annotation { "Feature Type Name" : "Feature", "Feature Type Description" : "" }
export const myFeature = defineFeature(function(context is Context, id is Id, definition is map)
    precondition{}
    {
        {
            var Q0;
            Q0=qCreatedBy(makeId("Top.planeOp"),FACE);
            var sketch = newSketch(context, id + "F0", { "sketchPlane" : qUnion([Q0])});
            skLineSegment(sketch, "E0.bottom", {"start": v(-4999.5, -4999.5) * mm, "end": v(4999.5, -4999.5) * mm});
            skLineSegment(sketch, "E0.top", {"start": v(-4999.5, 4999.5) * mm, "end": v(4999.5, 4999.5) * mm});
            skLineSegment(sketch, "E0.left", {"start": v(-4999.5, -4999.5) * mm, "end": v(-4999.5, 4999.5) * mm});
            skLineSegment(sketch, "E0.right", {"start": v(4999.5, -4999.5) * mm, "end": v(4999.5, 4999.5) * mm});
            skLineSegment(sketch, "E1", {"start": v(-4999.5, 4999.5) * mm, "end": v(4999.5, -4999.5) * mm, "construction": true});
            skSolve(sketch);
        }
        {
            var Q0;
            Q0=makeQuery(id+"F0.imprint","IMPRINT",FACE,{"disambiguationData":[TD([[makeQuery(id+"F0.imprint","IMPRINT",EDGE,{"derivedFrom":sQuery(id+"F0.wireOp",EDGE,"E0.bottom")}),1.0]])]});
            extrude(context, id + "F1", {"entities" : qUnion([Q0]), "endBound" : BoundingType.SYMMETRIC, "depth" : 9999 * mm, "offsetDistance" : 25 * mm});
        }
        {
            var Q0;
            Q0=qCreatedBy(makeId("Front.planeOp"),FACE);
            var sketch = newSketch(context, id + "F2", { "sketchPlane" : qUnion([Q0])});
            skLineSegment(sketch, "E2", {"start": v(0, 0) * mm, "end": v(0, 17.55) * mm});
            skLineSegment(sketch, "E3", {"start": v(0, 63.5) * mm, "end": v(-40, 63.5) * mm, "construction": true});
            skLineSegment(sketch, "E4", {"start": v(-40, 77.05) * mm, "end": v(-40, 49.95) * mm});
            skLineSegment(sketch, "E5", {"start": v(-27.76, 35.2) * mm, "end": v(-12.24, 32.3) * mm});
            skLineSegment(sketch, "E6", {"start": v(-27.76, 91.8) * mm, "end": v(-12.24, 94.7) * mm});
            skLineSegment(sketch, "E7.trimOffspring", {"start": v(0, 109.45) * mm, "end": v(0, 127) * mm});
            skLineSegment(sketch, "E8", {"start": v(0, 97) * mm, "end": v(0, 63.5) * mm, "construction": true});
            skLineSegment(sketch, "E9", {"start": v(0, 63.5) * mm, "end": v(0, 30) * mm, "construction": true});
            skPoint(sketch, "E10.visualSharp", {"position": v(0, 97) * mm});
            skArc(sketch, "E10.filletArc", {"start": v(-12.24, 94.7) * mm, "mid": v(-3.46, 99.87) * mm, "end": v(0, 109.45) * mm});
            skPoint(sketch, "E11.visualSharp", {"position": v(-40, 89.5) * mm});
            skArc(sketch, "E11.filletArc", {"start": v(-27.76, 91.8) * mm, "mid": v(-36.54, 86.63) * mm, "end": v(-40, 77.05) * mm});
            skPoint(sketch, "E12.visualSharp", {"position": v(-40, 37.5) * mm});
            skArc(sketch, "E12.filletArc", {"start": v(-40, 49.95) * mm, "mid": v(-36.54, 40.37) * mm, "end": v(-27.76, 35.2) * mm});
            skPoint(sketch, "E13.visualSharp", {"position": v(0, 30) * mm});
            skArc(sketch, "E13.filletArc", {"start": v(0, 17.55) * mm, "mid": v(-3.46, 27.13) * mm, "end": v(-12.24, 32.3) * mm});
            skLineSegment(sketch, "E14.0", {"start": v(-4, 109.45) * mm, "end": v(-4, 127) * mm});
            skArc(sketch, "E14.1", {"start": v(-12.97, 98.64) * mm, "mid": v(-6.54, 102.42) * mm, "end": v(-4, 109.45) * mm});
            skLineSegment(sketch, "E14.2", {"start": v(-28.5, 95.73) * mm, "end": v(-12.97, 98.64) * mm});
            skArc(sketch, "E14.3", {"start": v(-28.5, 95.73) * mm, "mid": v(-39.62, 89.19) * mm, "end": v(-44, 77.05) * mm});
            skLineSegment(sketch, "E14.4", {"start": v(-44, 77.05) * mm, "end": v(-44, 49.95) * mm});
            skLineSegment(sketch, "E14.5", {"start": v(-4, 0) * mm, "end": v(-4, 17.55) * mm});
            skArc(sketch, "E14.6", {"start": v(-4, 17.55) * mm, "mid": v(-6.54, 24.58) * mm, "end": v(-12.97, 28.36) * mm});
            skLineSegment(sketch, "E14.7", {"start": v(-28.5, 31.27) * mm, "end": v(-12.97, 28.36) * mm});
            skArc(sketch, "E14.8", {"start": v(-44, 49.95) * mm, "mid": v(-39.62, 37.81) * mm, "end": v(-28.5, 31.27) * mm});
            skLineSegment(sketch, "E15", {"start": v(0, 127) * mm, "end": v(-4, 127) * mm});
            skLineSegment(sketch, "E16", {"start": v(-4, 0) * mm, "end": v(0, 0) * mm});
            skSolve(sketch);
        }
        {
            var Q0;
            Q0=qCreatedBy(makeId("Front.planeOp"),FACE);
            cPlane(context, id + "F3", {"entities" : qUnion([Q0]), "cplaneType" : CPlaneType.OFFSET, "offset" : 60 * mm, "width" : 150 * mm, "height" : 150 * mm});
        }
        {
            var Q0;
            Q0=qCreatedBy(id+"F3.planeOp",FACE);
            var sketch = newSketch(context, id + "F4", { "sketchPlane" : qUnion([Q0])});
            skLineSegment(sketch, "E17.0", {"start": v(0, 0) * mm, "end": v(0, 17.55) * mm});
            skLineSegment(sketch, "E17.1", {"start": v(0, 63.5) * mm, "end": v(-40, 63.5) * mm, "construction": true});
            skLineSegment(sketch, "E17.2", {"start": v(-40, 77.05) * mm, "end": v(-40, 49.95) * mm, "construction": true});
            skLineSegment(sketch, "E17.3", {"start": v(-27.76, 35.2) * mm, "end": v(-12.24, 32.3) * mm, "construction": true});
            skLineSegment(sketch, "E17.4", {"start": v(-27.76, 91.8) * mm, "end": v(-12.24, 94.7) * mm, "construction": true});
            skLineSegment(sketch, "E17.5", {"start": v(0, 109.45) * mm, "end": v(0, 127) * mm});
            skLineSegment(sketch, "E17.6", {"start": v(0, 97) * mm, "end": v(0, 63.5) * mm});
            skLineSegment(sketch, "E17.7", {"start": v(0, 63.5) * mm, "end": v(0, 30) * mm});
            skPoint(sketch, "E17.8", {"position": v(0, 97) * mm});
            skArc(sketch, "E17.9", {"start": v(-12.24, 94.7) * mm, "mid": v(-3.46, 99.87) * mm, "end": v(0, 109.45) * mm});
            skPoint(sketch, "E17.10", {"position": v(-40, 89.5) * mm});
            skArc(sketch, "E17.11", {"start": v(-27.76, 91.8) * mm, "mid": v(-36.54, 86.63) * mm, "end": v(-40, 77.05) * mm, "construction": true});
            skPoint(sketch, "E17.12", {"position": v(-40, 37.5) * mm});
            skArc(sketch, "E17.13", {"start": v(-40, 49.95) * mm, "mid": v(-36.54, 40.37) * mm, "end": v(-27.76, 35.2) * mm, "construction": true});
            skPoint(sketch, "E17.14", {"position": v(0, 30) * mm});
            skArc(sketch, "E17.15", {"start": v(0, 17.55) * mm, "mid": v(-3.46, 27.13) * mm, "end": v(-12.24, 32.3) * mm});
            skLineSegment(sketch, "E17.16", {"start": v(-4, 109.45) * mm, "end": v(-4, 127) * mm});
            skArc(sketch, "E17.17", {"start": v(-12.42, 98.76) * mm, "mid": v(-6.36, 102.64) * mm, "end": v(-4, 109.45) * mm});
            skLineSegment(sketch, "E17.18", {"start": v(-28.5, 95.73) * mm, "end": v(-12.97, 98.64) * mm, "construction": true});
            skArc(sketch, "E17.19", {"start": v(-28.5, 95.73) * mm, "mid": v(-39.62, 89.19) * mm, "end": v(-44, 77.05) * mm, "construction": true});
            skLineSegment(sketch, "E17.20", {"start": v(-44, 77.05) * mm, "end": v(-44, 49.95) * mm, "construction": true});
            skLineSegment(sketch, "E17.21", {"start": v(-4, 0) * mm, "end": v(-4, 17.55) * mm});
            skArc(sketch, "E17.22", {"start": v(-4, 17.55) * mm, "mid": v(-6.36, 24.36) * mm, "end": v(-12.42, 28.24) * mm});
            skLineSegment(sketch, "E17.23", {"start": v(-28.5, 31.27) * mm, "end": v(-12.97, 28.36) * mm, "construction": true});
            skArc(sketch, "E17.24", {"start": v(-44, 49.95) * mm, "mid": v(-39.62, 37.81) * mm, "end": v(-28.5, 31.27) * mm, "construction": true});
            skLineSegment(sketch, "E17.25", {"start": v(0, 127) * mm, "end": v(-4, 127) * mm});
            skLineSegment(sketch, "E17.26", {"start": v(-4, 0) * mm, "end": v(0, 0) * mm});
            skLineSegment(sketch, "E18", {"start": v(-12.24, 32.3) * mm, "end": v(-33.69, 36.32) * mm});
            skLineSegment(sketch, "E19", {"start": v(-50, 55.97) * mm, "end": v(-50, 63.5) * mm});
            skLineSegment(sketch, "E20", {"start": v(-12.24, 94.7) * mm, "end": v(-33.69, 90.68) * mm});
            skLineSegment(sketch, "E21", {"start": v(-50, 71.03) * mm, "end": v(-50, 63.5) * mm});
            skLineSegment(sketch, "E22", {"start": v(-12.42, 98.76) * mm, "end": v(-35.16, 93.26) * mm});
            skLineSegment(sketch, "E23", {"start": v(-52, 71.88) * mm, "end": v(-52, 55.12) * mm});
            skLineSegment(sketch, "E24", {"start": v(-35.16, 33.74) * mm, "end": v(-12.42, 28.24) * mm});
            skLineSegment(sketch, "E25", {"start": v(-50, 87.62) * mm, "end": v(-50.47, 89.57) * mm, "construction": true});
            skPoint(sketch, "E26.orphan", {"position": v(-12.97, 98.64) * mm});
            skLineSegment(sketch, "E27", {"start": v(-50, 39.38) * mm, "end": v(-50.47, 37.43) * mm, "construction": true});
            skPoint(sketch, "E28.orphan", {"position": v(-12.97, 28.36) * mm});
            skPoint(sketch, "E29.visualSharp", {"position": v(-50, 87.63) * mm});
            skArc(sketch, "E29.filletArc", {"start": v(-33.69, 90.68) * mm, "mid": v(-45.4, 83.8) * mm, "end": v(-50, 71.03) * mm});
            skPoint(sketch, "E30.visualSharp", {"position": v(-50, 39.38) * mm});
            skArc(sketch, "E30.filletArc", {"start": v(-50, 55.97) * mm, "mid": v(-45.4, 43.2) * mm, "end": v(-33.69, 36.32) * mm});
            skPoint(sketch, "E31.visualSharp", {"position": v(-52, 89.2) * mm});
            skArc(sketch, "E31.filletArc", {"start": v(-35.16, 93.26) * mm, "mid": v(-47.29, 85.49) * mm, "end": v(-52, 71.88) * mm});
            skPoint(sketch, "E32.visualSharp", {"position": v(-52, 37.8) * mm});
            skArc(sketch, "E32.filletArc", {"start": v(-52, 55.12) * mm, "mid": v(-47.29, 41.51) * mm, "end": v(-35.16, 33.74) * mm});
            skSolve(sketch);
        }
        {
            var Q0;
            Q0 = qSketchRegion(id + "F2", true);
            var Q1;
            Q1 = qSketchRegion(id + "F4", true);
            loft(context, id + "F5", {"sheetProfilesArray" : [{ "sheetProfileEntities" : qUnion([Q0]) }, { "sheetProfileEntities" : qUnion([Q1]) }]});
        }
        {
            var Q0;
            Q0=makeQuery(id+"F5.opLoft","CAP_FACE",FACE,{"disambiguationData":[OSD([makeQuery(id+"F4.imprint","IMPRINT",FACE,{"disambiguationData":[TD([[makeQuery(id+"F4.imprint","IMPRINT",EDGE,{"derivedFrom":sQuery(id+"F4.wireOp",EDGE,"E17.0")}),1.0]])]})])],"isStart":true});
            var Q1;
            Q1=makeQuery(id+"F5.opLoft","CAP_FACE",FACE,{"disambiguationData":[OSD([makeQuery(id+"F2.imprint","IMPRINT",FACE,{"disambiguationData":[TD([[makeQuery(id+"F2.imprint","IMPRINT",EDGE,{"derivedFrom":sQuery(id+"F2.wireOp",EDGE,"E2")}),1.0]])]})])],"isStart":true});
            cPlane(context, id + "F6", {"entities" : qUnion([Q0, Q1]), "cplaneType" : CPlaneType.MID_PLANE, "offset" : 25 * mm, "width" : 150 * mm, "height" : 150 * mm});
        }
        {
            var Q0;
            Q0=qCreatedBy(id+"F6.planeOp",FACE);
            var sketch = newSketch(context, id + "F7", { "sketchPlane" : qUnion([Q0])});
            skLineSegment(sketch, "E33.0", {"start": v(0, 109.45) * mm, "end": v(0, 127) * mm, "construction": true});
            skLineSegment(sketch, "E34", {"start": v(0, 120.76) * mm, "end": v(0, 118.22) * mm});
            skLineSegment(sketch, "E35", {"start": v(0, 120.76) * mm, "end": v(-2, 120.76) * mm});
            skLineSegment(sketch, "E36", {"start": v(-2, 120.76) * mm, "end": v(-5, 123.37) * mm});
            skLineSegment(sketch, "E37", {"start": v(0, 118.22) * mm, "end": v(-5, 118.22) * mm});
            skLineSegment(sketch, "E38", {"start": v(-5, 118.22) * mm, "end": v(-5, 123.37) * mm});
            skLineSegment(sketch, "E39", {"start": v(0, 127) * mm, "end": v(0, 0) * mm, "construction": true});
            skLineSegment(sketch, "E40", {"start": v(0, 63.5) * mm, "end": v(-27.8, 63.5) * mm, "construction": true});
            skLineSegment(sketch, "E41.MirrorCS", {"start": v(0, 6.24) * mm, "end": v(-2, 6.24) * mm});
            skLineSegment(sketch, "E42.MirrorCS", {"start": v(0, 8.78) * mm, "end": v(-5, 8.78) * mm});
            skLineSegment(sketch, "E43.MirrorCS", {"start": v(-2, 6.24) * mm, "end": v(-5, 3.63) * mm});
            skLineSegment(sketch, "E44.MirrorCS", {"start": v(0, 6.24) * mm, "end": v(0, 8.78) * mm});
            skLineSegment(sketch, "E45.MirrorCS", {"start": v(-5, 8.78) * mm, "end": v(-5, 3.63) * mm});
            skSolve(sketch);
        }
        {
            var Q0;
            Q0=makeQuery(id+"F7.imprint","IMPRINT",FACE,{"disambiguationData":[TD([[makeQuery(id+"F7.imprint","IMPRINT",EDGE,{"derivedFrom":sQuery(id+"F7.wireOp",EDGE,"E34")}),-1.0]])]});
            var Q1;
            Q1=sQuery(id+"F7.wireOp",EDGE,"E37");
            revolve(context, id + "F8", {"operationType" : NewBodyOperationType.REMOVE, "surfaceOperationType" : NewSurfaceOperationType.NEW, "entities" : qUnion([Q0]), "axis" : qUnion([Q1]), "revolveType" : RevolveType.FULL, "oppositeDirection" : true});
        }
        {
            var Q0;
            Q0=makeQuery(id+"F7.imprint","IMPRINT",FACE,{"disambiguationData":[TD([[makeQuery(id+"F7.imprint","IMPRINT",EDGE,{"derivedFrom":sQuery(id+"F7.wireOp",EDGE,"E41.MirrorCS")}),-1.0]])]});
            var Q1;
            Q1=sQuery(id+"F7.wireOp",EDGE,"E42.MirrorCS");
            revolve(context, id + "F9", {"operationType" : NewBodyOperationType.REMOVE, "surfaceOperationType" : NewSurfaceOperationType.NEW, "entities" : qUnion([Q0]), "axis" : qUnion([Q1]), "revolveType" : RevolveType.FULL, "oppositeDirection" : true});
        }
        {
            var Q0;
            Q0=makeQuery(id+"F5.opLoft","MID_CAP_EDGE",EDGE,{"disambiguationData":[OSD([sQuery(id+"F4.wireOp",EDGE,"E17.5"),sQuery(id+"F4.wireOp",EDGE,"E17.16"),sQuery(id+"F4.wireOp",EDGE,"E17.25")])],"capPos":1.0});
            var Q1;
            Q1=makeQuery(id+"F5.opLoft","MID_CAP_EDGE",EDGE,{"disambiguationData":[OSD([sQuery(id+"F2.wireOp",EDGE,"E7.trimOffspring"),sQuery(id+"F2.wireOp",EDGE,"E14.0"),sQuery(id+"F2.wireOp",EDGE,"E15")])],"capPos":0.0});
            var Q2;
            Q2=makeQuery(id+"F5.opLoft","MID_CAP_EDGE",EDGE,{"disambiguationData":[OSD([sQuery(id+"F4.wireOp",EDGE,"E17.0"),sQuery(id+"F4.wireOp",EDGE,"E17.21"),sQuery(id+"F4.wireOp",EDGE,"E17.26")])],"capPos":1.0});
            var Q3;
            Q3=makeQuery(id+"F5.opLoft","MID_CAP_EDGE",EDGE,{"disambiguationData":[OSD([sQuery(id+"F2.wireOp",EDGE,"E2"),sQuery(id+"F2.wireOp",EDGE,"E14.5"),sQuery(id+"F2.wireOp",EDGE,"E16")])],"capPos":0.0});
            fillet(context, id + "F10", {"entities" : qUnion([Q0, Q1, Q2, Q3]), "tangentPropagation" : true, "radius" : 15 * mm, "defaultsChanged" : false, "vertexSettings" : [], "allowEdgeOverflow" : false});
        }
        {
            var Q0;
            Q0=makeQuery(id+"F5.opLoft","SWEPT_EDGE",EDGE,{"disambiguationData":[OSD([sQuery(id+"F2.wireOp",EDGE,"E14.0"),sQuery(id+"F2.wireOp",EDGE,"E15"),sQuery(id+"F4.wireOp",EDGE,"E17.16"),sQuery(id+"F4.wireOp",EDGE,"E17.25")])]});
            var Q1;
            Q1=makeQuery(id+"F5.opLoft","MID_CAP_EDGE",EDGE,{"disambiguationData":[OSD([sQuery(id+"F4.wireOp",EDGE,"E19"),sQuery(id+"F4.wireOp",EDGE,"E21"),sQuery(id+"F4.wireOp",EDGE,"E30.filletArc")])],"capPos":1.0});
            fillet(context, id + "F11", {"entities" : qUnion([Q0, Q1]), "tangentPropagation" : true, "radius" : 0.9 * mm, "defaultsChanged" : true, "vertexSettings" : [], "allowEdgeOverflow" : false});
        }
    });